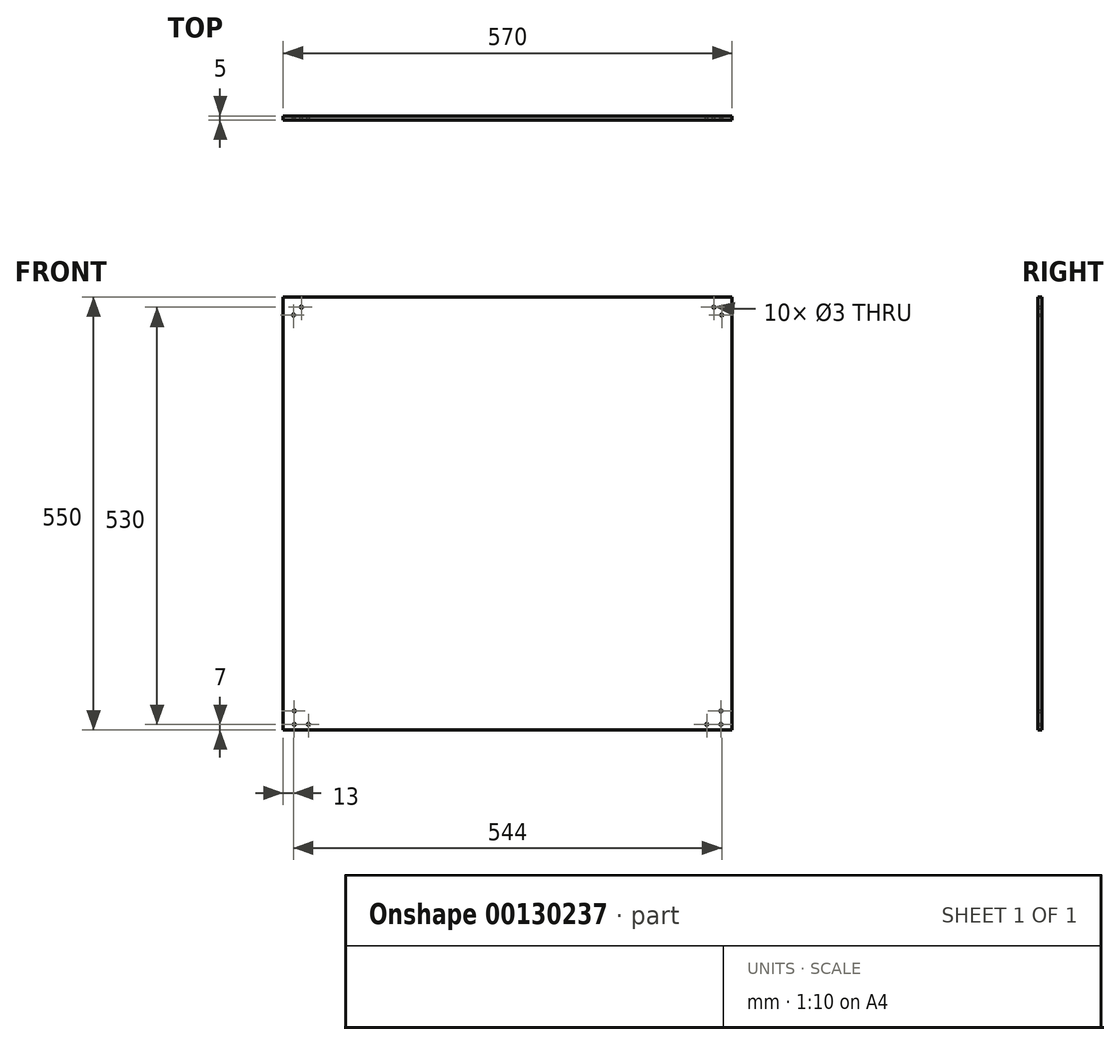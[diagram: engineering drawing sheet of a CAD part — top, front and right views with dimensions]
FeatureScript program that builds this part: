
annotation { "Feature Type Name" : "Feature", "Feature Type Description" : "" }
export const myFeature = defineFeature(function(context is Context, id is Id, definition is map)
    precondition{}
    {
        {
            var Q0;
            Q0=qCreatedBy(makeId("Front.planeOp"),FACE);
            var sketch = newSketch(context, id + "F0", { "sketchPlane" : qUnion([Q0])});
            skLineSegment(sketch, "E0.bottom", {"start": v(-285, -275) * mm, "end": v(285, -275) * mm});
            skLineSegment(sketch, "E0.top", {"start": v(-285, 275) * mm, "end": v(285, 275) * mm});
            skLineSegment(sketch, "E0.left", {"start": v(-285, -275) * mm, "end": v(-285, 275) * mm});
            skLineSegment(sketch, "E0.right", {"start": v(285, -275) * mm, "end": v(285, 275) * mm});
            skPoint(sketch, "E0.middle", {"position": v(0, 0) * mm});
            skCircle(sketch, "E1", {"center": v(-271, -251) * mm, "radius": 1.5 * mm});
            skCircle(sketch, "E2", {"center": v(-253, -268) * mm, "radius": 1.5 * mm});
            skCircle(sketch, "E3", {"center": v(-271, -268) * mm, "radius": 1.5 * mm});
            skCircle(sketch, "E4.MirrorC", {"center": v(271, -251) * mm, "radius": 1.5 * mm});
            skCircle(sketch, "E5.MirrorC", {"center": v(271, -268) * mm, "radius": 1.5 * mm});
            skCircle(sketch, "E6.MirrorC", {"center": v(253, -268) * mm, "radius": 1.5 * mm});
            skCircle(sketch, "E7", {"center": v(-262, 262) * mm, "radius": 1.5 * mm});
            skCircle(sketch, "E8", {"center": v(-272, 252) * mm, "radius": 1.5 * mm});
            skCircle(sketch, "E9.MirrorC", {"center": v(262, 262) * mm, "radius": 1.5 * mm});
            skCircle(sketch, "E10.MirrorC", {"center": v(272, 252) * mm, "radius": 1.5 * mm});
            skSolve(sketch);
        }
        {
            var Q0;
            Q0=makeQuery(id+"F0.imprint","IMPRINT",FACE,{"disambiguationData":[TD([[makeQuery(id+"F0.imprint","IMPRINT",EDGE,{"derivedFrom":sQuery(id+"F0.wireOp",EDGE,"E0.bottom")}),1.0]])]});
            extrude(context, id + "F1", {"entities" : qUnion([Q0]), "endBound" : BoundingType.SYMMETRIC, "depth" : 5 * mm});
        }
    });
